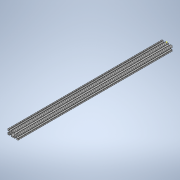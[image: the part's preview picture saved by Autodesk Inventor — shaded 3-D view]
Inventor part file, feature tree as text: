
AUTODESK INVENTOR PART (.ipt)
format: ipt  version: 2020 (Build 240168000, 168)  size: 333,824 bytes
history: native  units: in
note: dims shown in document units (in); Inventor stores cm internally (conversion verified against a paired STEP export)
features: sketch x2, extrude x1
ambient origin geometry x8: Origin, YZ Plane, XZ Plane, XY Plane, X Axis, Y Axis, Z Axis, Center Point
bodies: Solid1 (feature_tree)
feature tree (3):
  extrude  "Extrusion1"  [1 undecoded]
  sketch  "Sketch2"
  sketch  "Sketch1"  dims[d0=29.0in d1=0.0in]
note: 1 required parameter value undecoded (feature->parameter linkage not recoverable at this tier; creation-order binding heuristic only, values carry confidence <= 0.55)
